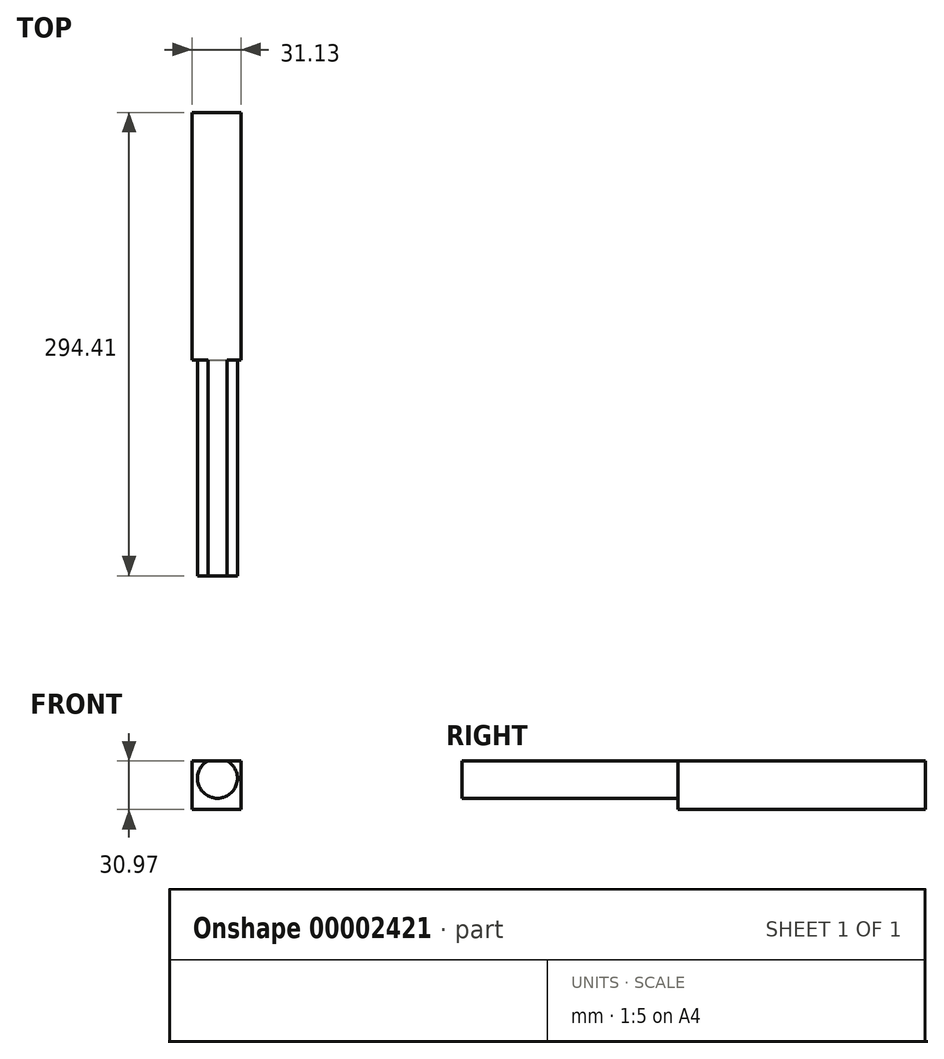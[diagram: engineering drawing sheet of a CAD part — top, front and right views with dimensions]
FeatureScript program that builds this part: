
annotation { "Feature Type Name" : "Feature", "Feature Type Description" : "" }
export const myFeature = defineFeature(function(context is Context, id is Id, definition is map)
    precondition{}
    {
        {
            var Q0;
            Q0=qCreatedBy(makeId("Front.planeOp"),FACE);
            var sketch = newSketch(context, id + "F0", { "sketchPlane" : qUnion([Q0])});
            skLineSegment(sketch, "E0.bottom", {"start": v(14.28, 11.1) * mm, "end": v(45.41, 11.1) * mm});
            skLineSegment(sketch, "E0.top", {"start": v(14.28, -19.87) * mm, "end": v(45.41, -19.87) * mm});
            skLineSegment(sketch, "E0.left", {"start": v(14.28, 11.1) * mm, "end": v(14.28, -19.87) * mm});
            skLineSegment(sketch, "E0.right", {"start": v(45.41, 11.1) * mm, "end": v(45.41, -19.87) * mm});
            skSolve(sketch);
        }
        {
            var Q0;
            Q0=makeQuery(id+"F0.imprint","IMPRINT",FACE,{"disambiguationData":[TD([[makeQuery(id+"F0.imprint","IMPRINT",EDGE,{"derivedFrom":sQuery(id+"F0.wireOp",EDGE,"E0.bottom")}),-1.0]])]});
            extrude(context, id + "F1", {"entities" : qUnion([Q0]), "depth" : 157.27 * mm});
        }
        {
            var Q0;
            Q0=makeQuery(id+"F1.opExtrude","CAP_FACE",FACE,{"disambiguationData":[OSD([sQuery(id+"F0.wireOp",EDGE,"E0.bottom"),sQuery(id+"F0.wireOp",EDGE,"E0.top"),sQuery(id+"F0.wireOp",EDGE,"E0.left"),sQuery(id+"F0.wireOp",EDGE,"E0.right")])],"isStart":false});
            var sketch = newSketch(context, id + "F2", { "sketchPlane" : qUnion([Q0])});
            skCircle(sketch, "E1", {"center": v(30.47, 0) * mm, "radius": 12.67 * mm});
            skSolve(sketch);
        }
        {
            var Q0;
            {var subQ0=makeQuery(id+"F1.opExtrude","CAP_EDGE",EDGE,{"disambiguationData":[OSD([sQuery(id+"F0.wireOp",EDGE,"E0.bottom")])],"isStart":false});var subQ1=sQuery(id+"F2.wireOp",EDGE,"E1");var subQ3=makeQuery(id+"F2.imprint","INTERSECT",VERTEX,{"disambiguationData":[OD(0.0)],"derivedFrom":[subQ0,subQ1]});Q0=makeQuery(id+"F2.imprint","IMPRINT",FACE,{"disambiguationData":[TD([[makeQuery(id+"F2.imprint","IMPRINT",EDGE,{"disambiguationData":[TD([[subQ3,-1.0]])],"derivedFrom":subQ1}),1.0]])]});}
            extrude(context, id + "F3", {"entities" : qUnion([Q0]), "operationType" : NewBodyOperationType.ADD, "depth" : 137.14 * mm});
        }
    });
